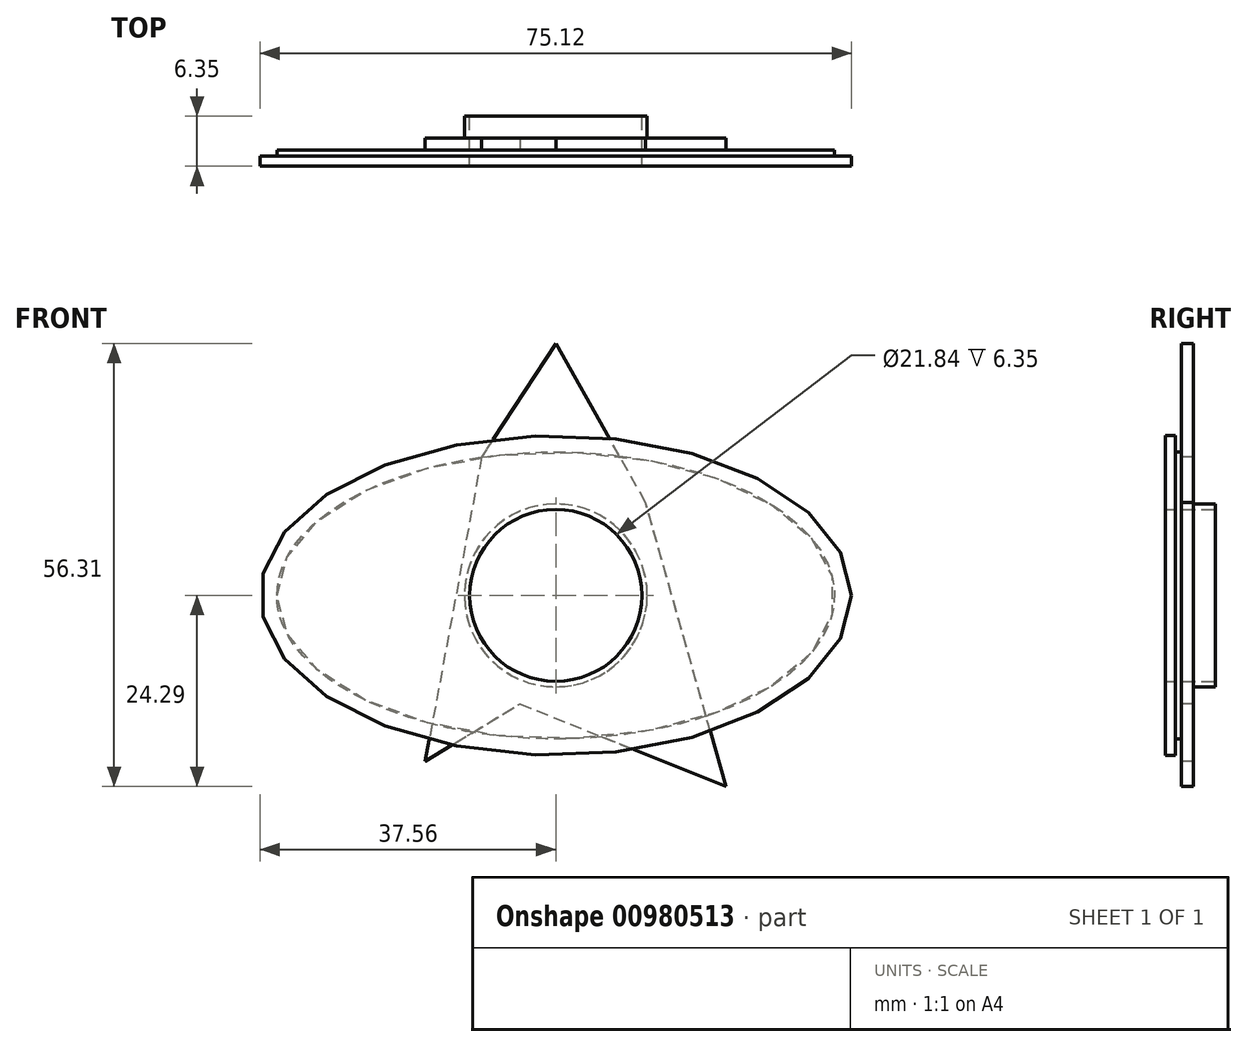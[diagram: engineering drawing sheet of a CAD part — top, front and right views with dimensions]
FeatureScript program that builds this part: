
annotation { "Feature Type Name" : "Feature", "Feature Type Description" : "" }
export const myFeature = defineFeature(function(context is Context, id is Id, definition is map)
    precondition{}
    {
        {
            var Q0;
            Q0=qCreatedBy(makeId("Front.planeOp"),FACE);
            var sketch = newSketch(context, id + "F0", { "sketchPlane" : qUnion([Q0])});
            skEllipse(sketch, "E0", {"center": v(0, 0) * mm, "majorRadius": 37.56 * mm, "minorRadius": 20.3 * mm, "majorAxis": v(1, 0)});
            skSolve(sketch);
        }
        {
            var Q0;
            Q0=makeQuery(id+"F0.imprint","IMPRINT",FACE,{"disambiguationData":[TD([[makeQuery(id+"F0.imprint","IMPRINT",EDGE,{"derivedFrom":sQuery(id+"F0.wireOp",EDGE,"E0")}),1.0]])]});
            extrude(context, id + "F1", {"entities" : qUnion([Q0]), "depth" : 0.76 * mm, "offsetDistance" : 25.4 * mm});
        }
        {
            var Q0;
            Q0=makeQuery(id+"F1.opExtrude","CAP_FACE",FACE,{"disambiguationData":[OSD([sQuery(id+"F0.wireOp",EDGE,"E0")])],"isStart":true});
            var sketch = newSketch(context, id + "F2", { "sketchPlane" : qUnion([Q0])});
            skEllipse(sketch, "E1", {"center": v(0, 0) * mm, "majorRadius": 35.42 * mm, "minorRadius": 18.22 * mm, "majorAxis": v(1, 0)});
            skSolve(sketch);
        }
        {
            var Q0;
            Q0=makeQuery(id+"F2.imprint","IMPRINT",FACE,{"disambiguationData":[TD([[makeQuery(id+"F2.imprint","IMPRINT",EDGE,{"derivedFrom":sQuery(id+"F2.wireOp",EDGE,"E1")}),1.0]])]});
            extrude(context, id + "F3", {"entities" : qUnion([Q0]), "operationType" : NewBodyOperationType.ADD, "depth" : 0.76 * mm, "offsetDistance" : 25.4 * mm});
        }
        {
            var Q0;
            Q0=makeQuery(id+"F1.opExtrude","CAP_FACE",FACE,{"disambiguationData":[OSD([sQuery(id+"F0.wireOp",EDGE,"E0")])],"isStart":false});
            extrude(context, id + "F4", {"entities" : qUnion([Q0]), "operationType" : NewBodyOperationType.ADD, "depth" : 0.5 * mm, "offsetDistance" : 25.4 * mm});
        }
        {
            var Q0;
            Q0=makeQuery(id+"F3.opExtrude","CAP_FACE",FACE,{"disambiguationData":[OSD([sQuery(id+"F2.wireOp",EDGE,"E1")])],"isStart":false});
            var sketch = newSketch(context, id + "F5", { "sketchPlane" : qUnion([Q0])});
            skLineSegment(sketch, "E2", {"start": v(-21.62, -24.29) * mm, "end": v(-11.4, 11.8) * mm});
            skLineSegment(sketch, "E3", {"start": v(-11.4, 11.8) * mm, "end": v(0, 32.02) * mm});
            skLineSegment(sketch, "E4", {"start": v(0, 32.02) * mm, "end": v(9.43, 17.56) * mm});
            skLineSegment(sketch, "E5", {"start": v(9.43, 17.56) * mm, "end": v(16.59, -21.09) * mm});
            skLineSegment(sketch, "E6", {"start": v(16.59, -21.09) * mm, "end": v(4.57, -13.78) * mm});
            skLineSegment(sketch, "E7", {"start": v(4.57, -13.78) * mm, "end": v(-21.62, -24.29) * mm});
            skSolve(sketch);
        }
        {
            var Q0;
            {var subQ8=sQuery(id+"F5.wireOp",EDGE,"E3");var subQ9=sQuery(id+"F5.wireOp",EDGE,"E2");var subQ10=makeQuery(id+"F5.imprint","INTERSECT",VERTEX,{"derivedFrom":[subQ9,subQ8]});Q0=makeQuery(id+"F5.imprint","IMPRINT",FACE,{"disambiguationData":[TD([[makeQuery(id+"F5.imprint","IMPRINT",EDGE,{"disambiguationData":[TD([[subQ10,1.0]])],"derivedFrom":subQ9}),-1.0]])]});}
            var Q1;
            {var subQ0=sQuery(id+"F5.wireOp",EDGE,"E4");Q1=makeQuery(id+"F5.imprint","IMPRINT",FACE,{"disambiguationData":[TD([[makeQuery(id+"F5.imprint","IMPRINT",EDGE,{"derivedFrom":subQ0}),-1.0]])]});}
            var Q2;
            {var subQ0=sQuery(id+"F5.wireOp",EDGE,"E7");var subQ1=sQuery(id+"F5.wireOp",EDGE,"E2");var subQ2=makeQuery(id+"F5.imprint","INTERSECT",VERTEX,{"derivedFrom":[subQ1,subQ0]});Q2=makeQuery(id+"F5.imprint","IMPRINT",FACE,{"disambiguationData":[TD([[makeQuery(id+"F5.imprint","IMPRINT",EDGE,{"disambiguationData":[TD([[subQ2,-1.0]])],"derivedFrom":subQ1}),-1.0]])]});}
            var Q3;
            {var subQ0=sQuery(id+"F5.wireOp",EDGE,"E6");var subQ1=sQuery(id+"F5.wireOp",EDGE,"E5");var subQ2=makeQuery(id+"F5.imprint","INTERSECT",VERTEX,{"derivedFrom":[subQ1,subQ0]});Q3=makeQuery(id+"F5.imprint","IMPRINT",FACE,{"disambiguationData":[TD([[makeQuery(id+"F5.imprint","IMPRINT",EDGE,{"disambiguationData":[TD([[subQ2,1.0]])],"derivedFrom":subQ1}),-1.0]])]});}
            extrude(context, id + "F6", {"entities" : qUnion([Q0, Q1, Q2, Q3]), "operationType" : NewBodyOperationType.ADD, "depth" : 1.52 * mm, "offsetDistance" : 25.4 * mm});
        }
        {
            var Q0;
            Q0=makeQuery(id+"F6.opExtrude","CAP_FACE",FACE,{"disambiguationData":[OSD([sQuery(id+"F5.wireOp",EDGE,"E2"),sQuery(id+"F5.wireOp",EDGE,"E3"),sQuery(id+"F5.wireOp",EDGE,"E4"),sQuery(id+"F5.wireOp",EDGE,"E5"),sQuery(id+"F5.wireOp",EDGE,"E6"),sQuery(id+"F5.wireOp",EDGE,"E7")])],"isStart":false});
            var sketch = newSketch(context, id + "F7", { "sketchPlane" : qUnion([Q0])});
            skCircle(sketch, "E8", {"center": v(0, 0) * mm, "radius": 10.92 * mm});
            skSolve(sketch);
        }
        {
            var Q0;
            Q0=makeQuery(id+"F7.imprint","IMPRINT",FACE,{"disambiguationData":[TD([[makeQuery(id+"F7.imprint","IMPRINT",EDGE,{"derivedFrom":sQuery(id+"F7.wireOp",EDGE,"E8")}),1.0]])]});
            extrude(context, id + "F8", {"entities" : qUnion([Q0]), "operationType" : NewBodyOperationType.REMOVE, "oppositeDirection" : true, "depth" : 26.67 * mm, "offsetDistance" : 25.4 * mm});
        }
        {
            var Q0;
            Q0=qCreatedBy(makeId("Front.planeOp"),FACE);
            var sketch = newSketch(context, id + "F9", { "sketchPlane" : qUnion([Q0])});
            skCircle(sketch, "E9", {"center": v(0, 0) * mm, "radius": 11.61 * mm});
            skSolve(sketch);
        }
        {
            var Q0;
            Q0=makeQuery(id+"F9.imprint","IMPRINT",FACE,{"disambiguationData":[TD([[makeQuery(id+"F9.imprint","IMPRINT",EDGE,{"derivedFrom":sQuery(id+"F9.wireOp",EDGE,"E9")}),1.0]])]});
            extrude(context, id + "F10", {"entities" : qUnion([Q0]), "operationType" : NewBodyOperationType.ADD, "oppositeDirection" : true, "depth" : 5.08 * mm, "offsetDistance" : 25.4 * mm});
        }
        {
            var Q0;
            Q0=makeQuery(id+"F10.opExtrude","CAP_FACE",FACE,{"disambiguationData":[OSD([sQuery(id+"F9.wireOp",EDGE,"E9")])],"isStart":true});
            extrude(context, id + "F11", {"entities" : qUnion([Q0]), "operationType" : NewBodyOperationType.REMOVE, "oppositeDirection" : true, "depth" : 25.4 * mm, "offsetDistance" : 25.4 * mm});
        }
    });
